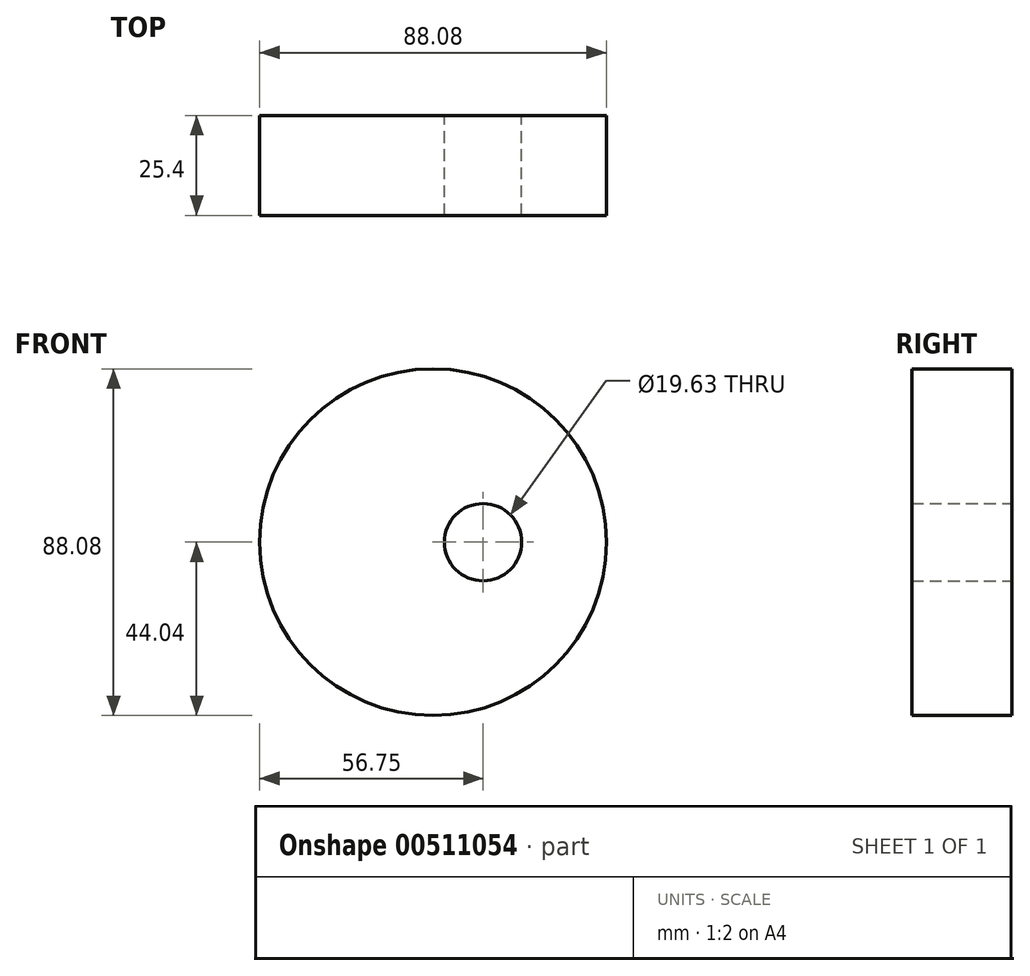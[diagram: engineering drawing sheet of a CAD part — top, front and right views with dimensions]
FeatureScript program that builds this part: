
annotation { "Feature Type Name" : "Feature", "Feature Type Description" : "" }
export const myFeature = defineFeature(function(context is Context, id is Id, definition is map)
    precondition{}
    {
        {
            var Q0;
            Q0=qCreatedBy(makeId("Front.planeOp"),FACE);
            var sketch = newSketch(context, id + "F0", { "sketchPlane" : qUnion([Q0])});
            skCircle(sketch, "E0", {"center": v(0, 0) * mm, "radius": 44.04 * mm});
            skCircle(sketch, "E1", {"center": v(12.7, 0) * mm, "radius": 9.82 * mm});
            skSolve(sketch);
        }
        {
            var Q0;
            Q0 = qSketchRegion(id + "F0", true);
            extrude(context, id + "F1", {"entities" : qUnion([Q0]), "endBound" : BoundingType.SYMMETRIC, "depth" : 25.4 * mm});
        }
    });
